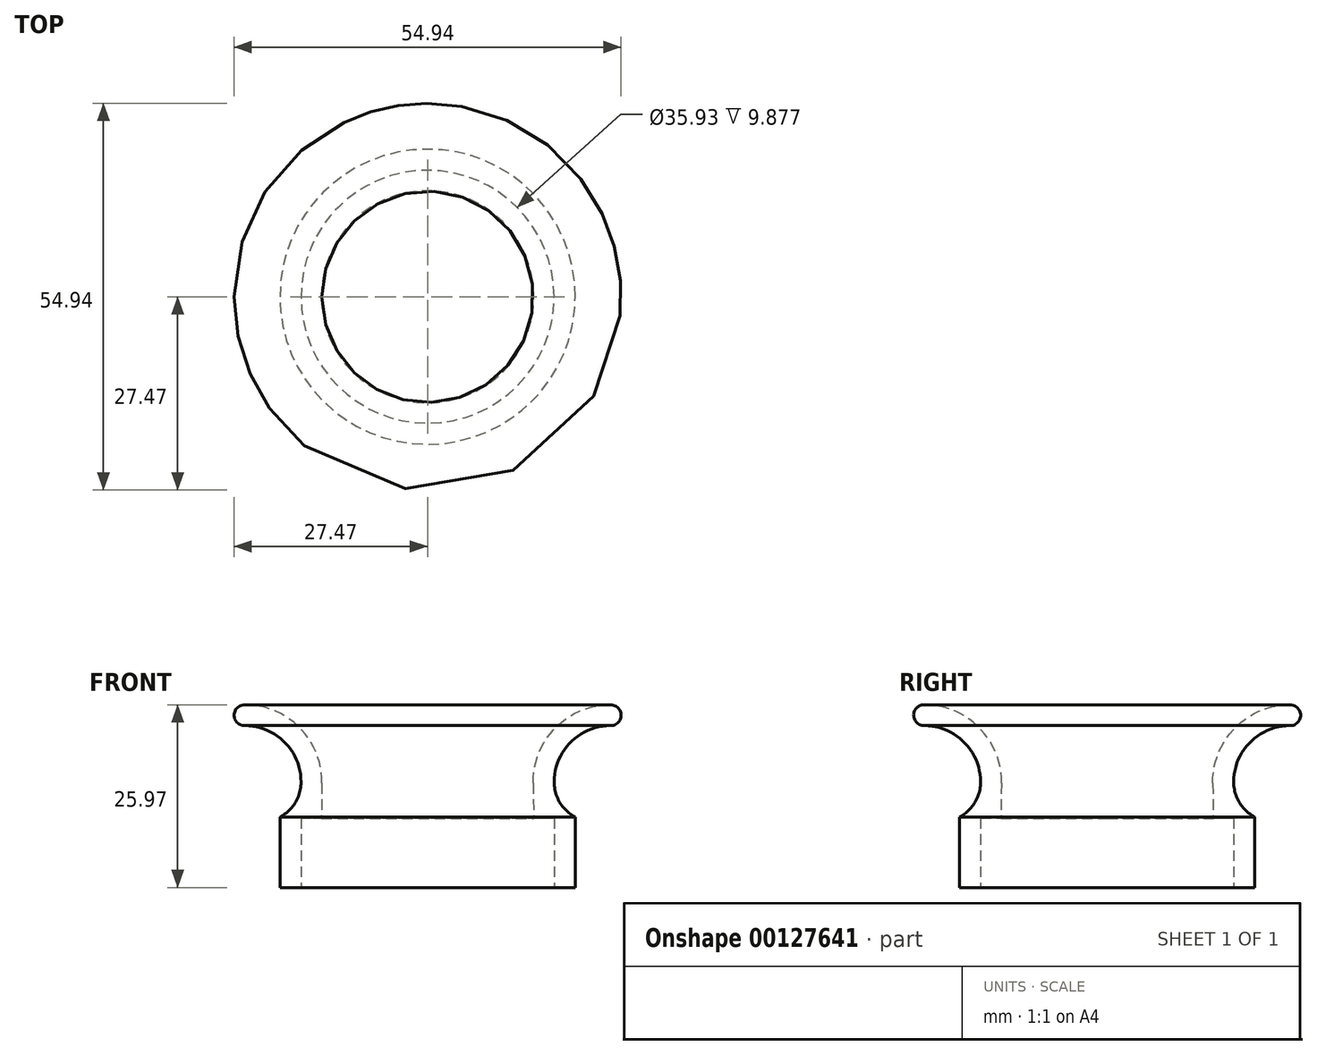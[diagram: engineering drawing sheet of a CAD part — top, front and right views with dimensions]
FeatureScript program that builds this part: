
annotation { "Feature Type Name" : "Feature", "Feature Type Description" : "" }
export const myFeature = defineFeature(function(context is Context, id is Id, definition is map)
    precondition{}
    {
        {
            var Q0;
            Q0=qCreatedBy(makeId("Front.planeOp"),FACE);
            var sketch = newSketch(context, id + "F0", { "sketchPlane" : qUnion([Q0])});
            skPoint(sketch, "E0.second.point", {"position": v(77.54, 19) * mm});
            skPoint(sketch, "E0.third.point", {"position": v(37.2, 56.24) * mm});
            skArc(sketch, "E1", {"start": v(10.97, 30.14) * mm, "mid": v(3.15, 26.86) * mm, "end": v(0, 19) * mm});
            skLineSegment(sketch, "E2", {"start": v(2.03, 0) * mm, "end": v(0, 0) * mm});
            skLineSegment(sketch, "E3", {"start": v(0, 0) * mm, "end": v(2.03, 0) * mm});
            skPoint(sketch, "E4.orphan", {"position": v(4.05, 0) * mm});
            skLineSegment(sketch, "E5", {"start": v(0, 0) * mm, "end": v(-15, 0) * mm});
            skLineSegment(sketch, "E6", {"start": v(-15, 0) * mm, "end": v(-15, 56.91) * mm});
            skArc(sketch, "E7", {"start": v(10.97, 27.17) * mm, "mid": v(5.3, 24.83) * mm, "end": v(2.97, 19.17) * mm});
            skCircle(sketch, "E8", {"center": v(9.55, 20) * mm, "radius": 0.83 * mm});
            skPoint(sketch, "E9.end.orphan", {"position": v(4.05, 10.65) * mm});
            skPoint(sketch, "E10.visualSharp", {"position": v(7.56, 0) * mm});
            skPoint(sketch, "E11.end.orphan", {"position": v(21.93, 19.17) * mm});
            skArc(sketch, "E12", {"start": v(10.97, 27.17) * mm, "mid": v(12.47, 28.65) * mm, "end": v(10.97, 30.14) * mm});
            skLineSegment(sketch, "E13", {"start": v(0, 19) * mm, "end": v(0.08, 14) * mm});
            skLineSegment(sketch, "E14", {"start": v(0.08, 14) * mm, "end": v(2.97, 14.04) * mm});
            skLineSegment(sketch, "E15", {"start": v(2.97, 14.04) * mm, "end": v(2.97, 14.17) * mm});
            skLineSegment(sketch, "E16", {"start": v(2.97, 14.17) * mm, "end": v(2.97, 4.17) * mm});
            skLineSegment(sketch, "E17", {"start": v(2.97, 4.17) * mm, "end": v(5.97, 4.17) * mm});
            skLineSegment(sketch, "E18", {"start": v(5.97, 4.17) * mm, "end": v(5.97, 14.17) * mm});
            skArc(sketch, "E19", {"start": v(2.97, 19.17) * mm, "mid": v(3.77, 16.25) * mm, "end": v(5.97, 14.17) * mm});
            skSolve(sketch);
        }
        {
            var Q0;
            {var subQ0=sQuery(id+"F0.wireOp",EDGE,"E1");Q0=makeQuery(id+"F0.imprint","IMPRINT",FACE,{"disambiguationData":[TD([[makeQuery(id+"F0.imprint","IMPRINT",EDGE,{"derivedFrom":subQ0}),1.0]])]});}
            var Q1;
            {var subQ2=sQuery(id+"F0.wireOp",EDGE,"zA0rpZqB-saLa-AZ3N-ox9s-bJx4H0fNbBDQ");Q1=makeQuery(id+"F0.imprint","IMPRINT",FACE,{"disambiguationData":[TD([[makeQuery(id+"F0.imprint","IMPRINT",EDGE,{"derivedFrom":subQ2}),-1.0]])]});}
            var Q2;
            Q2=sQuery(id+"F0.wireOp",EDGE,"E6");
            revolve(context, id + "F1", {"entities" : qUnion([Q0, Q1]), "axis" : qUnion([Q2]), "revolveType" : RevolveType.FULL});
        }
        {
            var Q0;
            Q0=makeQuery(id+"F1.opRevolve","SWEPT_EDGE",EDGE,{"disambiguationData":[OSD([sQuery(id+"F0.wireOp",EDGE,"E1"),sQuery(id+"F0.wireOp",EDGE,"E11")])]});
            var Q1;
            Q1=makeQuery(id+"F1.opRevolve","SWEPT_EDGE",EDGE,{"disambiguationData":[OSD([sQuery(id+"F0.wireOp",EDGE,"E7"),sQuery(id+"F0.wireOp",EDGE,"E11")])]});
            fillet(context, id + "F2", {"entities" : qUnion([Q0, Q1]), "radius" : 1 * mm, "tangentPropagation" : true, "allowEdgeOverflow" : false});
        }
    });
